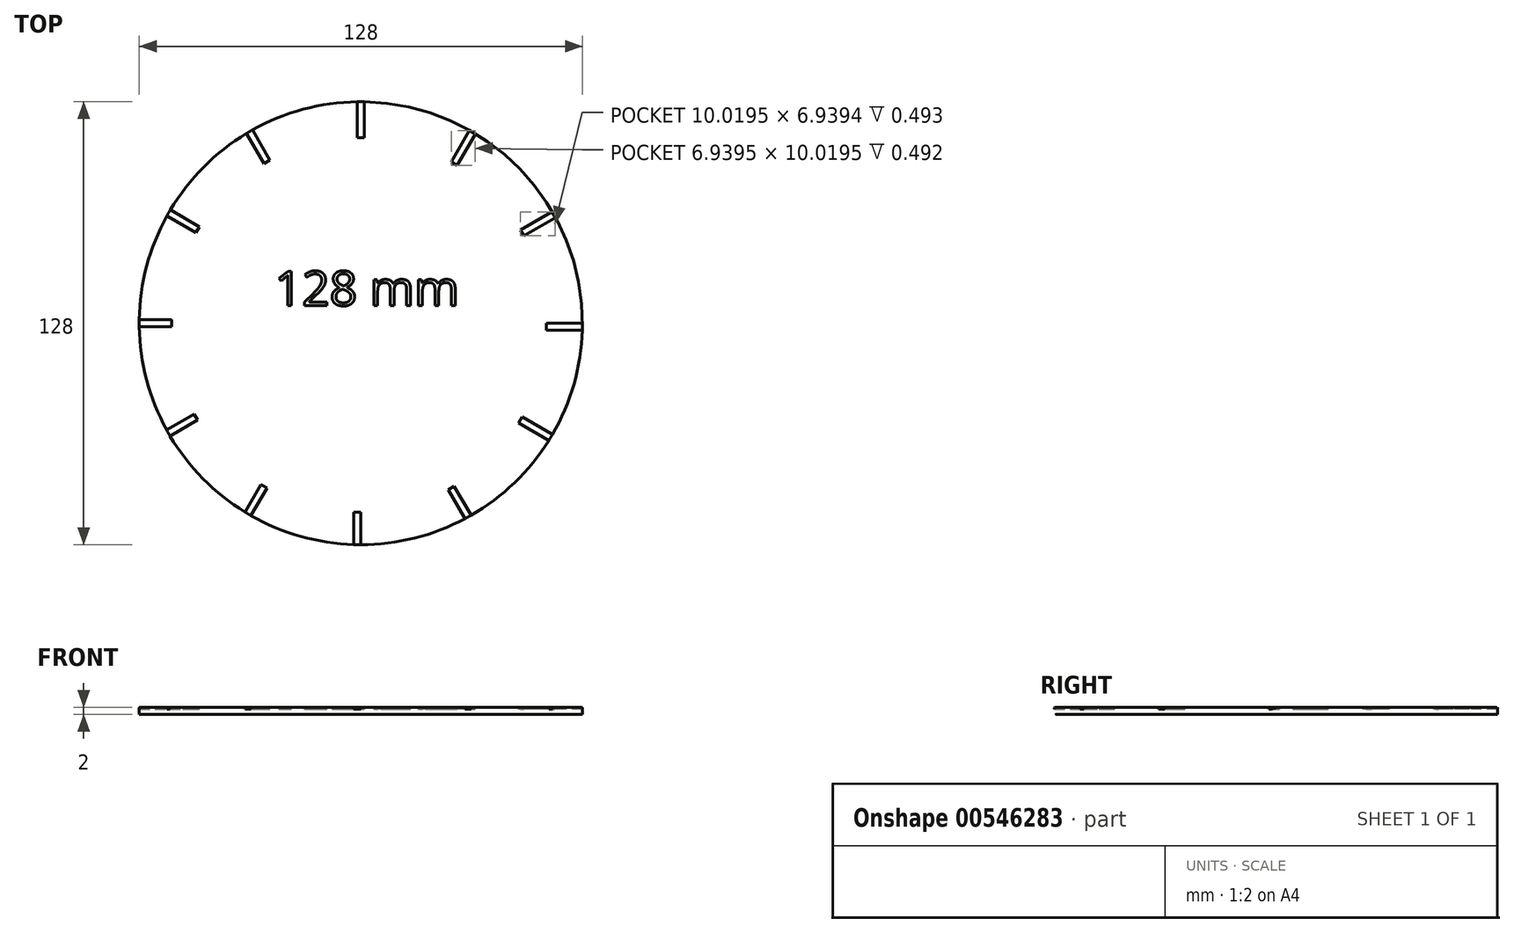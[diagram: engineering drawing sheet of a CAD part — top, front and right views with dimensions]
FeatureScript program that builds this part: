
annotation { "Feature Type Name" : "Feature", "Feature Type Description" : "" }
export const myFeature = defineFeature(function(context is Context, id is Id, definition is map)
    precondition{}
    {
        {
            var Q0;
            Q0=qCreatedBy(makeId("Top.planeOp"),FACE);
            var sketch = newSketch(context, id + "F0", { "sketchPlane" : qUnion([Q0])});
            skCircle(sketch, "E0", {"center": v(0, 0) * mm, "radius": 64 * mm});
            skSolve(sketch);
        }
        {
            var Q0;
            Q0=qSketchRegion(id+"F0",true);
            extrude(context, id + "F1", {"entities" : qUnion([Q0]), "depth" : 2 * mm, "offsetDistance" : 25 * mm});
        }
        {
            var Q0;
            Q0=makeQuery(id+"F1.opExtrude","CAP_FACE",FACE,{"disambiguationData":[OSD([sQuery(id+"F0.wireOp",EDGE,"E0")])],"isStart":false});
            var sketch = newSketch(context, id + "F2", { "sketchPlane" : qUnion([Q0])});
            skLineSegment(sketch, "E1.bottom", {"start": v(-1, 64) * mm, "end": v(1, 64) * mm});
            skLineSegment(sketch, "E1.top", {"start": v(-1, 53.58) * mm, "end": v(1, 53.58) * mm});
            skLineSegment(sketch, "E1.left", {"start": v(-1, 64) * mm, "end": v(-1, 53.58) * mm});
            skLineSegment(sketch, "E1.right", {"start": v(1, 64) * mm, "end": v(1, 53.58) * mm});
            skLineSegment(sketch, "E2.1.0", {"start": v(-33.18, 55.1) * mm, "end": v(-27.97, 46.08) * mm});
            skLineSegment(sketch, "E2.1.1", {"start": v(-31.45, 56.1) * mm, "end": v(-26.24, 47.08) * mm});
            skLineSegment(sketch, "E2.1.2", {"start": v(-27.97, 46.08) * mm, "end": v(-26.24, 47.08) * mm});
            skLineSegment(sketch, "E2.1.3", {"start": v(-33.18, 55.1) * mm, "end": v(-31.45, 56.1) * mm});
            skLineSegment(sketch, "E2.2.0", {"start": v(-56.6, 31.31) * mm, "end": v(-47.58, 26.1) * mm});
            skLineSegment(sketch, "E2.2.1", {"start": v(-55.6, 33.05) * mm, "end": v(-46.58, 27.84) * mm});
            skLineSegment(sketch, "E2.2.2", {"start": v(-47.58, 26.1) * mm, "end": v(-46.58, 27.84) * mm});
            skLineSegment(sketch, "E2.2.3", {"start": v(-56.6, 31.31) * mm, "end": v(-55.6, 33.05) * mm});
            skPoint(sketch, "E2.center", {"position": v(-0.5, -0.5) * mm});
            skLineSegment(sketch, "E3.2.3.0", {"start": v(-65, -1) * mm, "end": v(-54.58, -1) * mm});
            skLineSegment(sketch, "E3.3.3.0", {"start": v(-65, 1) * mm, "end": v(-54.58, 1) * mm});
            skLineSegment(sketch, "E3.6.3.0", {"start": v(-54.58, -1) * mm, "end": v(-54.58, 1) * mm});
            skLineSegment(sketch, "E3.9.3.0", {"start": v(-65, -1) * mm, "end": v(-65, 1) * mm});
            skLineSegment(sketch, "E3.2.4.0", {"start": v(-56.1, -33.18) * mm, "end": v(-47.08, -27.97) * mm});
            skLineSegment(sketch, "E3.3.4.0", {"start": v(-57.1, -31.45) * mm, "end": v(-48.08, -26.24) * mm});
            skLineSegment(sketch, "E3.6.4.0", {"start": v(-47.08, -27.97) * mm, "end": v(-48.08, -26.24) * mm});
            skLineSegment(sketch, "E3.9.4.0", {"start": v(-56.1, -33.18) * mm, "end": v(-57.1, -31.45) * mm});
            skLineSegment(sketch, "E3.2.5.0", {"start": v(-32.31, -56.6) * mm, "end": v(-27.1, -47.58) * mm});
            skLineSegment(sketch, "E3.3.5.0", {"start": v(-34.05, -55.6) * mm, "end": v(-28.84, -46.58) * mm});
            skLineSegment(sketch, "E3.6.5.0", {"start": v(-27.1, -47.58) * mm, "end": v(-28.84, -46.58) * mm});
            skLineSegment(sketch, "E3.9.5.0", {"start": v(-32.31, -56.6) * mm, "end": v(-34.05, -55.6) * mm});
            skLineSegment(sketch, "E3.2.6.0", {"start": v(0, -65) * mm, "end": v(0, -54.58) * mm});
            skLineSegment(sketch, "E3.3.6.0", {"start": v(-2, -65) * mm, "end": v(-2, -54.58) * mm});
            skLineSegment(sketch, "E3.6.6.0", {"start": v(0, -54.58) * mm, "end": v(-2, -54.58) * mm});
            skLineSegment(sketch, "E3.9.6.0", {"start": v(0, -65) * mm, "end": v(-2, -65) * mm});
            skLineSegment(sketch, "E3.2.7.0", {"start": v(32.18, -56.1) * mm, "end": v(26.97, -47.08) * mm});
            skLineSegment(sketch, "E3.3.7.0", {"start": v(30.45, -57.1) * mm, "end": v(25.24, -48.08) * mm});
            skLineSegment(sketch, "E3.6.7.0", {"start": v(26.97, -47.08) * mm, "end": v(25.24, -48.08) * mm});
            skLineSegment(sketch, "E3.9.7.0", {"start": v(32.18, -56.1) * mm, "end": v(30.45, -57.1) * mm});
            skLineSegment(sketch, "E3.2.8.0", {"start": v(55.6, -32.31) * mm, "end": v(46.58, -27.1) * mm});
            skLineSegment(sketch, "E3.3.8.0", {"start": v(54.6, -34.05) * mm, "end": v(45.58, -28.84) * mm});
            skLineSegment(sketch, "E3.6.8.0", {"start": v(46.58, -27.1) * mm, "end": v(45.58, -28.84) * mm});
            skLineSegment(sketch, "E3.9.8.0", {"start": v(55.6, -32.31) * mm, "end": v(54.6, -34.05) * mm});
            skLineSegment(sketch, "E3.2.9.0", {"start": v(64, 0) * mm, "end": v(53.58, 0) * mm});
            skLineSegment(sketch, "E3.3.9.0", {"start": v(64, -2) * mm, "end": v(53.58, -2) * mm});
            skLineSegment(sketch, "E3.6.9.0", {"start": v(53.58, 0) * mm, "end": v(53.58, -2) * mm});
            skLineSegment(sketch, "E3.9.9.0", {"start": v(64, 0) * mm, "end": v(64, -2) * mm});
            skLineSegment(sketch, "E3.2.10.0", {"start": v(55.1, 32.18) * mm, "end": v(46.08, 26.97) * mm});
            skLineSegment(sketch, "E3.3.10.0", {"start": v(56.1, 30.45) * mm, "end": v(47.08, 25.24) * mm});
            skLineSegment(sketch, "E3.6.10.0", {"start": v(46.08, 26.97) * mm, "end": v(47.08, 25.24) * mm});
            skLineSegment(sketch, "E3.9.10.0", {"start": v(55.1, 32.18) * mm, "end": v(56.1, 30.45) * mm});
            skLineSegment(sketch, "E3.2.11.0", {"start": v(31.31, 55.6) * mm, "end": v(26.1, 46.58) * mm});
            skLineSegment(sketch, "E3.3.11.0", {"start": v(33.05, 54.6) * mm, "end": v(27.84, 45.58) * mm});
            skLineSegment(sketch, "E3.6.11.0", {"start": v(26.1, 46.58) * mm, "end": v(27.84, 45.58) * mm});
            skLineSegment(sketch, "E3.9.11.0", {"start": v(31.31, 55.6) * mm, "end": v(33.05, 54.6) * mm});
            skSolve(sketch);
        }
        {
            var Q0;
            Q0=qSketchRegion(id+"F2",true);
            extrude(context, id + "F3", {"entities" : qUnion([Q0]), "operationType" : NewBodyOperationType.REMOVE, "oppositeDirection" : true, "depth" : 0.5 * mm, "offsetDistance" : 25 * mm});
        }
        {
            var Q0;
            Q0=makeQuery(id+"F1.opExtrude","CAP_FACE",FACE,{"disambiguationData":[OSD([sQuery(id+"F0.wireOp",EDGE,"E0")])],"isStart":false});
            var sketch = newSketch(context, id + "F4", { "sketchPlane" : qUnion([Q0])});
            skText(sketch, "E4", { "text": "128 mm\n", "fontName": "OpenSans-Regular.ttf"});
            const initialGuessF4  = {"E4": [-0.02488, 0.0051, 1, 0, 0.01]};
            skSetInitialGuess(sketch, initialGuessF4);
            skSolve(sketch);
        }
        {
            var Q0;
            Q0=qSketchRegion(id+"F4",true);
            extrude(context, id + "F5", {"entities" : qUnion([Q0]), "operationType" : NewBodyOperationType.REMOVE, "oppositeDirection" : true, "depth" : 0.5 * mm, "offsetDistance" : 25 * mm});
        }
        {
            var Q0;
            {var subQ0=sQuery(id+"F0.wireOp",EDGE,"E0");Q0=makeQuery(id+"F3.boolean.opBoolean","SPLIT",EDGE,{"disambiguationData":[TD([makeQuery(id+"F3.opExtrude","SWEPT_FACE",FACE,{"disambiguationData":[OSD([sQuery(id+"F2.wireOp",EDGE,"E3.2.6.0")])]})])],"derivedFrom":makeQuery(id+"F1.opExtrude","CAP_EDGE",EDGE,{"disambiguationData":[OSD([subQ0])],"isStart":false})});}
            var Q1;
            {var subQ0=sQuery(id+"F0.wireOp",EDGE,"E0");Q1=makeQuery(id+"F3.boolean.opBoolean","SPLIT",EDGE,{"disambiguationData":[TD([makeQuery(id+"F3.opExtrude","SWEPT_FACE",FACE,{"disambiguationData":[OSD([sQuery(id+"F2.wireOp",EDGE,"E3.2.5.0")])]})])],"derivedFrom":makeQuery(id+"F1.opExtrude","CAP_EDGE",EDGE,{"disambiguationData":[OSD([subQ0])],"isStart":false})});}
            var Q2;
            {var subQ0=sQuery(id+"F0.wireOp",EDGE,"E0");Q2=makeQuery(id+"F3.boolean.opBoolean","SPLIT",EDGE,{"disambiguationData":[TD([makeQuery(id+"F3.opExtrude","SWEPT_FACE",FACE,{"disambiguationData":[OSD([sQuery(id+"F2.wireOp",EDGE,"E3.2.4.0")])]})])],"derivedFrom":makeQuery(id+"F1.opExtrude","CAP_EDGE",EDGE,{"disambiguationData":[OSD([subQ0])],"isStart":false})});}
            var Q3;
            {var subQ0=sQuery(id+"F0.wireOp",EDGE,"E0");Q3=makeQuery(id+"F3.boolean.opBoolean","SPLIT",EDGE,{"disambiguationData":[TD([makeQuery(id+"F3.opExtrude","SWEPT_FACE",FACE,{"disambiguationData":[OSD([sQuery(id+"F2.wireOp",EDGE,"E3.2.3.0")])]})])],"derivedFrom":makeQuery(id+"F1.opExtrude","CAP_EDGE",EDGE,{"disambiguationData":[OSD([subQ0])],"isStart":false})});}
            var Q4;
            {var subQ0=sQuery(id+"F0.wireOp",EDGE,"E0");Q4=makeQuery(id+"F3.boolean.opBoolean","SPLIT",EDGE,{"disambiguationData":[TD([makeQuery(id+"F3.opExtrude","SWEPT_FACE",FACE,{"disambiguationData":[OSD([sQuery(id+"F2.wireOp",EDGE,"E2.2.0")])]})])],"derivedFrom":makeQuery(id+"F1.opExtrude","CAP_EDGE",EDGE,{"disambiguationData":[OSD([subQ0])],"isStart":false})});}
            var Q5;
            {var subQ0=sQuery(id+"F0.wireOp",EDGE,"E0");Q5=makeQuery(id+"F3.boolean.opBoolean","SPLIT",EDGE,{"disambiguationData":[TD([makeQuery(id+"F3.opExtrude","SWEPT_FACE",FACE,{"disambiguationData":[OSD([sQuery(id+"F2.wireOp",EDGE,"E3.2.7.0")])]})])],"derivedFrom":makeQuery(id+"F1.opExtrude","CAP_EDGE",EDGE,{"disambiguationData":[OSD([subQ0])],"isStart":false})});}
            var Q6;
            {var subQ0=sQuery(id+"F0.wireOp",EDGE,"E0");Q6=makeQuery(id+"F3.boolean.opBoolean","SPLIT",EDGE,{"disambiguationData":[TD([makeQuery(id+"F3.opExtrude","SWEPT_FACE",FACE,{"disambiguationData":[OSD([sQuery(id+"F2.wireOp",EDGE,"E3.2.8.0")])]})])],"derivedFrom":makeQuery(id+"F1.opExtrude","CAP_EDGE",EDGE,{"disambiguationData":[OSD([subQ0])],"isStart":false})});}
            var Q7;
            {var subQ0=sQuery(id+"F0.wireOp",EDGE,"E0");Q7=makeQuery(id+"F3.boolean.opBoolean","SPLIT",EDGE,{"disambiguationData":[TD([makeQuery(id+"F3.opExtrude","SWEPT_FACE",FACE,{"disambiguationData":[OSD([sQuery(id+"F2.wireOp",EDGE,"E3.2.9.0")])]})])],"derivedFrom":makeQuery(id+"F1.opExtrude","CAP_EDGE",EDGE,{"disambiguationData":[OSD([subQ0])],"isStart":false})});}
            var Q8;
            {var subQ0=sQuery(id+"F0.wireOp",EDGE,"E0");Q8=makeQuery(id+"F3.boolean.opBoolean","SPLIT",EDGE,{"disambiguationData":[TD([makeQuery(id+"F3.opExtrude","SWEPT_FACE",FACE,{"disambiguationData":[OSD([sQuery(id+"F2.wireOp",EDGE,"E3.2.10.0")])]})])],"derivedFrom":makeQuery(id+"F1.opExtrude","CAP_EDGE",EDGE,{"disambiguationData":[OSD([subQ0])],"isStart":false})});}
            var Q9;
            {var subQ0=sQuery(id+"F0.wireOp",EDGE,"E0");Q9=makeQuery(id+"F3.boolean.opBoolean","SPLIT",EDGE,{"disambiguationData":[TD([makeQuery(id+"F3.opExtrude","SWEPT_FACE",FACE,{"disambiguationData":[OSD([sQuery(id+"F2.wireOp",EDGE,"E1.right")])]})])],"derivedFrom":makeQuery(id+"F1.opExtrude","CAP_EDGE",EDGE,{"disambiguationData":[OSD([subQ0])],"isStart":false})});}
            var Q10;
            {var subQ0=sQuery(id+"F0.wireOp",EDGE,"E0");Q10=makeQuery(id+"F3.boolean.opBoolean","SPLIT",EDGE,{"disambiguationData":[TD([makeQuery(id+"F3.opExtrude","SWEPT_FACE",FACE,{"disambiguationData":[OSD([sQuery(id+"F2.wireOp",EDGE,"E1.left")])]})])],"derivedFrom":makeQuery(id+"F1.opExtrude","CAP_EDGE",EDGE,{"disambiguationData":[OSD([subQ0])],"isStart":false})});}
            var Q11;
            {var subQ0=sQuery(id+"F0.wireOp",EDGE,"E0");Q11=makeQuery(id+"F3.boolean.opBoolean","SPLIT",EDGE,{"disambiguationData":[TD([makeQuery(id+"F3.opExtrude","SWEPT_FACE",FACE,{"disambiguationData":[OSD([sQuery(id+"F2.wireOp",EDGE,"E2.1.0")])]})])],"derivedFrom":makeQuery(id+"F1.opExtrude","CAP_EDGE",EDGE,{"disambiguationData":[OSD([subQ0])],"isStart":false})});}
            fillet(context, id + "F6", {"entities" : qUnion([Q0, Q1, Q2, Q3, Q4, Q5, Q6, Q7, Q8, Q9, Q10, Q11]), "radius" : .25 * mm, "allowEdgeOverflow" : false});
        }
    });
